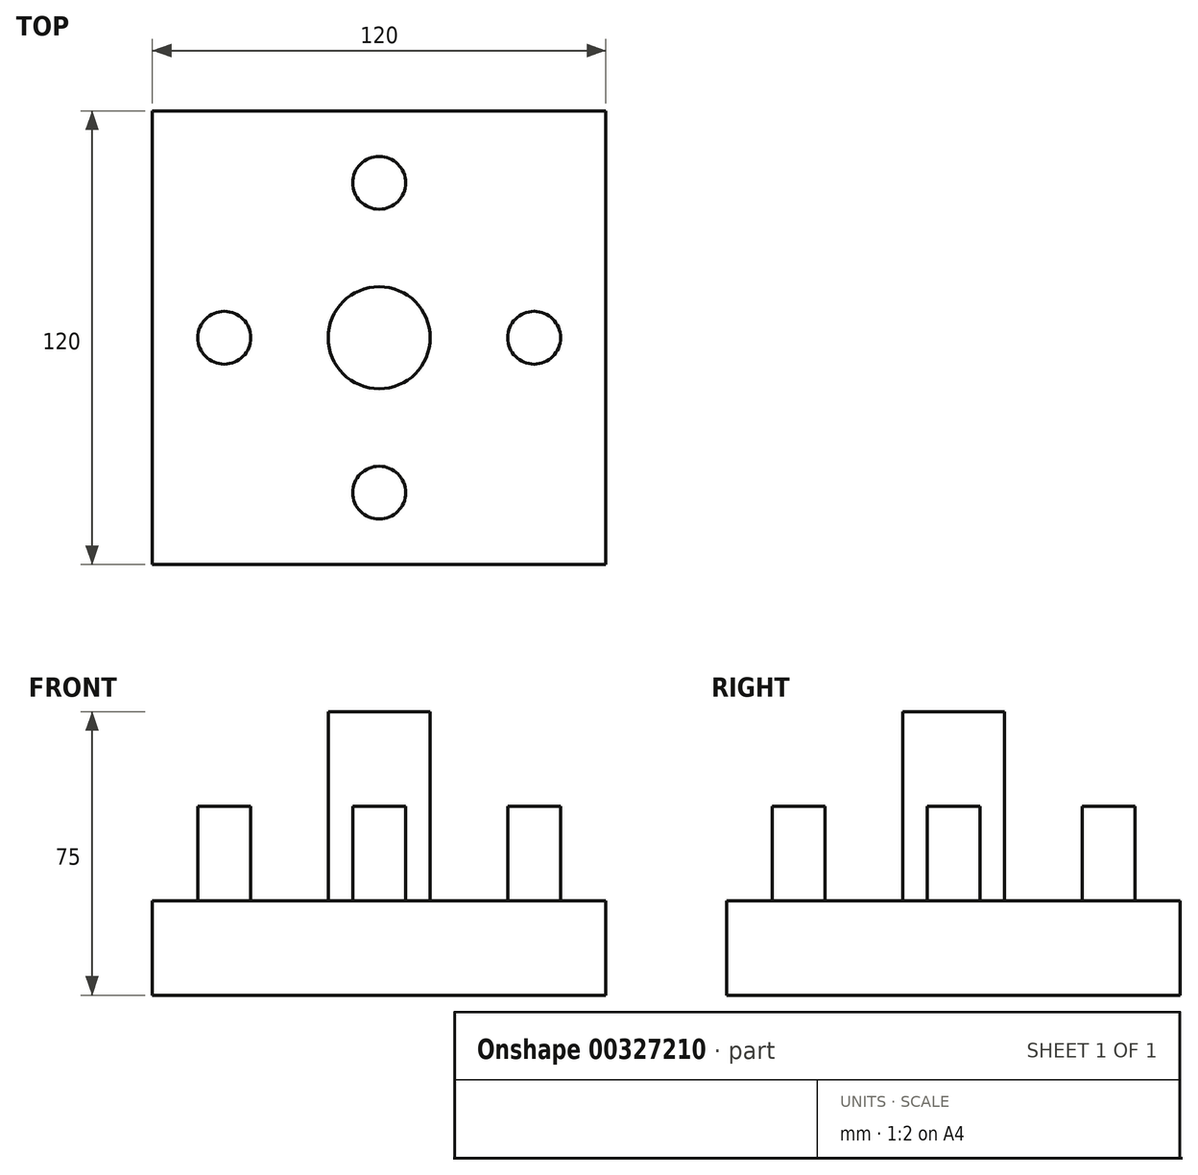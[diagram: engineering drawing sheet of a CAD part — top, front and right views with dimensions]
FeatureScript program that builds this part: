
annotation { "Feature Type Name" : "Feature", "Feature Type Description" : "" }
export const myFeature = defineFeature(function(context is Context, id is Id, definition is map)
    precondition{}
    {
        {
            var Q0;
            Q0=qCreatedBy(makeId("Top.planeOp"),FACE);
            var sketch = newSketch(context, id + "F0", { "sketchPlane" : qUnion([Q0])});
            skLineSegment(sketch, "E0.bottom", {"start": v(-60, 60) * mm, "end": v(60, 60) * mm});
            skLineSegment(sketch, "E0.top", {"start": v(-60, -60) * mm, "end": v(60, -60) * mm});
            skLineSegment(sketch, "E0.left", {"start": v(-60, 60) * mm, "end": v(-60, -60) * mm});
            skLineSegment(sketch, "E0.right", {"start": v(60, 60) * mm, "end": v(60, -60) * mm});
            skSolve(sketch);
        }
        {
            var Q0;
            Q0 = qSketchRegion(id + "F0", true);
            extrude(context, id + "F1", {"entities" : qUnion([Q0]), "depth" : 25 * mm});
        }
        {
            var Q0;
            Q0=makeQuery(id+"F1.opExtrude","CAP_FACE",FACE,{"disambiguationData":[OSD([sQuery(id+"F0.wireOp",EDGE,"E0.bottom"),sQuery(id+"F0.wireOp",EDGE,"E0.top"),sQuery(id+"F0.wireOp",EDGE,"E0.left"),sQuery(id+"F0.wireOp",EDGE,"E0.right")])],"isStart":false});
            var sketch = newSketch(context, id + "F2", { "sketchPlane" : qUnion([Q0])});
            skCircle(sketch, "E1", {"center": v(0, 41) * mm, "radius": 7 * mm});
            skCircle(sketch, "E2.1.0", {"center": v(-41, 0) * mm, "radius": 7 * mm});
            skCircle(sketch, "E2.2.0", {"center": v(0, -41) * mm, "radius": 7 * mm});
            skCircle(sketch, "E2.3.0", {"center": v(41, 0) * mm, "radius": 7 * mm});
            skPoint(sketch, "E2.center", {"position": v(0, 0) * mm});
            skSolve(sketch);
        }
        {
            var Q0;
            Q0 = qSketchRegion(id + "F2", true);
            extrude(context, id + "F3", {"entities" : qUnion([Q0]), "operationType" : NewBodyOperationType.ADD, "depth" : 25 * mm});
        }
        {
            var Q0;
            Q0=makeQuery(id+"F1.opExtrude","CAP_FACE",FACE,{"disambiguationData":[OSD([sQuery(id+"F0.wireOp",EDGE,"E0.bottom"),sQuery(id+"F0.wireOp",EDGE,"E0.top"),sQuery(id+"F0.wireOp",EDGE,"E0.left"),sQuery(id+"F0.wireOp",EDGE,"E0.right")])],"isStart":false});
            var sketch = newSketch(context, id + "F4", { "sketchPlane" : qUnion([Q0])});
            skCircle(sketch, "E3", {"center": v(0, 0) * mm, "radius": 13.5 * mm});
            skSolve(sketch);
        }
        {
            var Q0;
            Q0=makeQuery(id+"F4.imprint","IMPRINT",FACE,{"disambiguationData":[TD([[makeQuery(id+"F4.imprint","IMPRINT",EDGE,{"derivedFrom":sQuery(id+"F4.wireOp",EDGE,"E3")}),1.0]])]});
            extrude(context, id + "F5", {"entities" : qUnion([Q0]), "operationType" : NewBodyOperationType.ADD, "depth" : 50 * mm});
        }
    });
